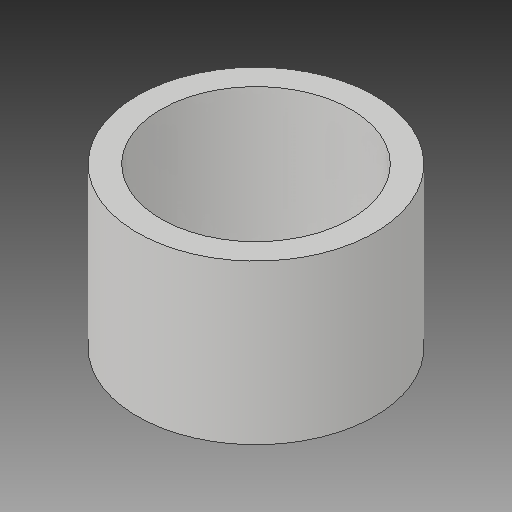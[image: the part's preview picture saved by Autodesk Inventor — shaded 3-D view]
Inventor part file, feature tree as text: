
AUTODESK INVENTOR PART (.ipt)
format: ipt  version: 2018.3 (Build 223284000, 284)  size: 88,064 bytes
history: native  units: mm
features: other x1, extrude x1, sketch x1
ambient origin geometry x8: Origin, YZ Plane, XZ Plane, XY Plane, X Axis, Y Axis, Z Axis, Center Point
bodies: Body1 (feature_tree)
feature tree (3):
  other  "ソリッド1"
  extrude  "押し出し1"  Depth=10.0mm
  sketch  "スケッチ1"
